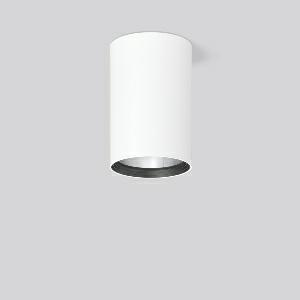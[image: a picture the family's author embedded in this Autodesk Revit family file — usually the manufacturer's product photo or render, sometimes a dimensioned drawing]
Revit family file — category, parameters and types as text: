
# Revit family: heledon_maxi_a_931216_002_2_26d2
name_source: partatom
category: Lighting Fixtures
units: mm (PartAtom-declared; Revit-internal decimal feet)

## family parameters
Cut with Voids When Loaded = No
Host = Face
Light Source = No
Part Type = Normal
Room Calculation Point = No
Round Connector Dimension = Use Diameter
Shared = No

## types (1)
- HELEDON maxi A (1 x LED Modul 927, 3050 lm, 2700)
    Apparent Load = 25 VA
    Approval mark = CE
    CIE Flux Codes = 100 100 100 100 100
    Color Rendering = 92
    Color Temperature = 2700
    Default Elevation = 1800 mm
    Description = Series: HELEDON maxi
Cylindrical surface-mounted downlight. Housing: die-cast aluminium, powder-coated. Internal ceiling frame polycarbonate with bayonet mounting. Black plastic ring and recessed LED to prevent glare from the side. Optical assembly with reflector made of MIRO-Silver with 98% total light reflection for outstanding efficiency - can be changed without tools. Best colour rendering index Ra>90. Suitable for Ceiling mounting. Easy installation with a separate ceiling frame with bayonet mounting and plug connection. Driver integrated. Connected via plug-in connector. High quality converter without flickering and stroboscopic effect. The following accessories can be mounted without use of tools: interchangeable lenses, decorative glasses, honeycomb louvre, clear and frosted diffusers, white interchangeable plastic ring. 
Colour: traffic white, matt (RAL 9016)
Diameter: 123 mm
Height: 183 mm
Lamp: LED
Socket: without socket
Colour temperature: 2700K
Colour rendering index (CRI): 92
System power: 25 W
Rated luminous flux: 3050 lm
Luminous efficiency: 122 lm/W
Control gear: Regulated power supply
Protection class: I
Type of protection: IP 20
    Height = 183 mm
    Lamp = 1 x LED Modul 927
    Lamp Light Flux = 3050 lm
    Lamp count = 1
    Length = 123 mm
    Lifetime = 50000 h
    Luminous efficacy = 122 lm/W
    Manufacturer = RZB
    ModVariant = No
    Model = 931216.002.2
    Mounting Place = Ceiling
    Mounting Type = Surface mounted
    Number of Poles = 1
    OnlyDefault = Yes
    Power Factor = 1
    Product Name = HELEDON maxi A
    Product group = Surface mounted downlights
    ProductGroupID = 302
    Protection Class = Protection class I
    Protection Degree = IP 20
    RLX_Detail_Level = 1
    RLX_Emergency_Light_Flux = 0 lm
    RLX_Emergency_Type = 0
    RLX_Emergency_Type_DB = No
    RlxData = <blob elided: 98077 chars, md5=7d20e02b>
    Socket = socket
    Standby Power = 0 W
    System Light Flux = 3050 lm
    System Power = 25 W
    Type Comments = Product without accessories
    Type Image = 931192.002.jpg
    URL = http://relux.com
    VarID = ---
    Voltage = 230 V
    Voltage Range = 220-240 V
    Weight = 0.00 kg
    Width = 0 mm  [stored 0 ft]

note: [stored X ft] marks values corroborated as IEEE doubles in the binary element streams (Revit-internal decimal feet)

## geometry (parser evidence)
native form markers: Blend x4, Sweep x11
no freeform markers — native parametric forms only
